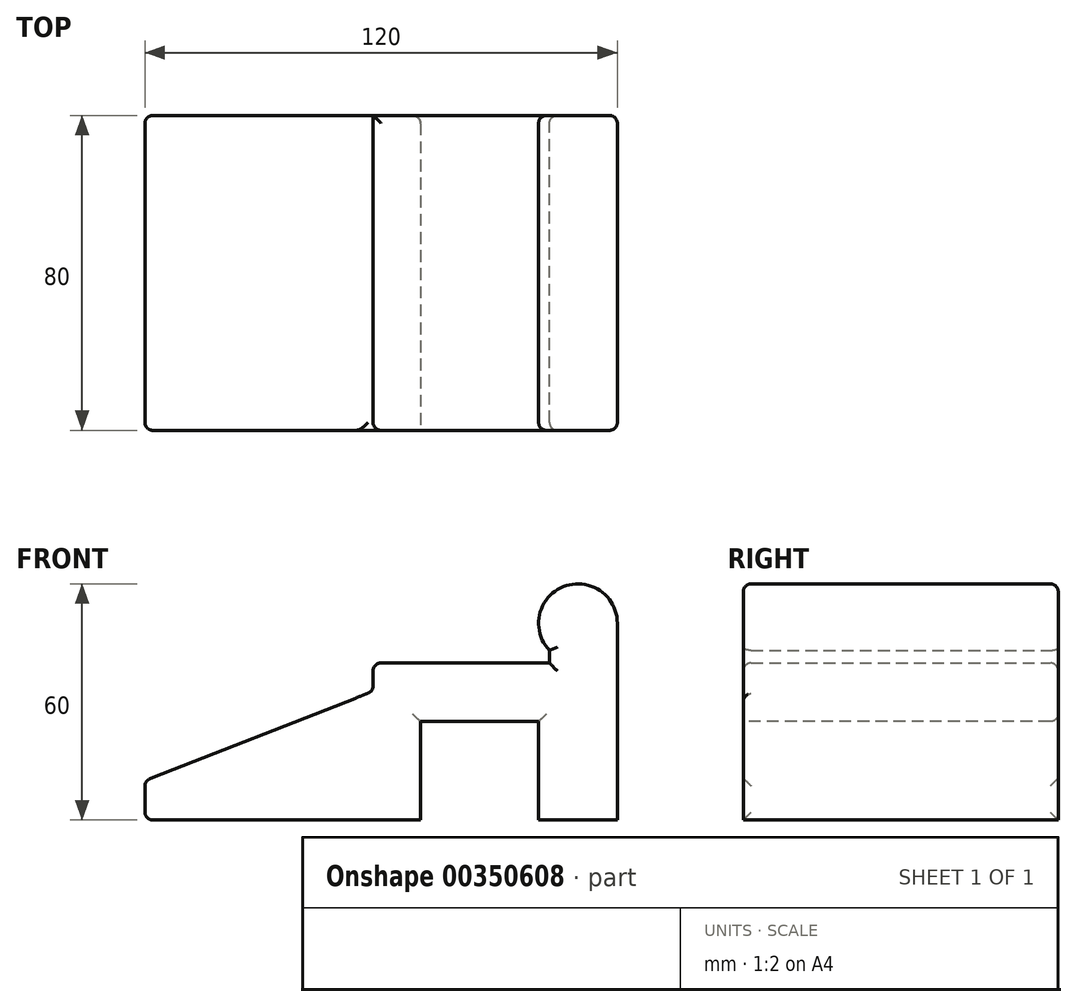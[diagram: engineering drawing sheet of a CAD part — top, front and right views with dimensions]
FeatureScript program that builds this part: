
annotation { "Feature Type Name" : "Feature", "Feature Type Description" : "" }
export const myFeature = defineFeature(function(context is Context, id is Id, definition is map)
    precondition{}
    {
        {
            var Q0;
            Q0=qCreatedBy(makeId("Front.planeOp"),FACE);
            var sketch = newSketch(context, id + "F0", { "sketchPlane" : qUnion([Q0])});
            skArc(sketch, "E0", {"start": v(112.98, 31.44) * mm, "mid": v(99.26, 40.72) * mm, "end": v(95.74, 24.54) * mm});
            skLineSegment(sketch, "E1", {"start": v(112.98, 31.44) * mm, "end": v(112.98, -18.56) * mm});
            skLineSegment(sketch, "E2", {"start": v(112.98, -18.56) * mm, "end": v(-7.02, -18.56) * mm});
            skLineSegment(sketch, "E3", {"start": v(-7.02, -8.56) * mm, "end": v(-7.02, -18.56) * mm});
            skLineSegment(sketch, "E4", {"start": v(95.74, 24.54) * mm, "end": v(95.74, 21.35) * mm});
            skLineSegment(sketch, "E5", {"start": v(50.93, 14.16) * mm, "end": v(50.93, 21.35) * mm});
            skLineSegment(sketch, "E6", {"start": v(50.93, 21.35) * mm, "end": v(95.74, 21.35) * mm});
            skLineSegment(sketch, "E7", {"start": v(-7.02, -8.56) * mm, "end": v(50.93, 14.16) * mm});
            skSolve(sketch);
        }
        {
            var Q0;
            Q0=makeQuery(id+"F0.imprint","IMPRINT",FACE,{"disambiguationData":[TD([[makeQuery(id+"F0.imprint","IMPRINT",EDGE,{"derivedFrom":sQuery(id+"F0.wireOp",EDGE,"E0")}),1.0]])]});
            extrude(context, id + "F1", {"entities" : qUnion([Q0]), "depth" : 80 * mm});
        }
        {
            var Q0;
            Q0=makeQuery(id+"F1.opExtrude","CAP_FACE",FACE,{"disambiguationData":[OSD([sQuery(id+"F0.wireOp",EDGE,"E0"),sQuery(id+"F0.wireOp",EDGE,"E1"),sQuery(id+"F0.wireOp",EDGE,"E2"),sQuery(id+"F0.wireOp",EDGE,"E3"),sQuery(id+"F0.wireOp",EDGE,"E4"),sQuery(id+"F0.wireOp",EDGE,"1WNvFodx-eBXk-6IQv-WaWy-YzUaJAq4HSbU"),sQuery(id+"F0.wireOp",EDGE,"E5"),sQuery(id+"F0.wireOp",EDGE,"E6")])],"isStart":false});
            var sketch = newSketch(context, id + "F2", { "sketchPlane" : qUnion([Q0])});
            skLineSegment(sketch, "E8.bottom", {"start": v(92.98, 6.44) * mm, "end": v(62.98, 6.44) * mm});
            skLineSegment(sketch, "E8.top", {"start": v(92.98, -18.56) * mm, "end": v(62.98, -18.56) * mm});
            skLineSegment(sketch, "E8.left", {"start": v(92.98, 6.44) * mm, "end": v(92.98, -18.56) * mm});
            skLineSegment(sketch, "E8.right", {"start": v(62.98, 6.44) * mm, "end": v(62.98, -18.56) * mm});
            skSolve(sketch);
        }
        {
            var Q0;
            Q0=makeQuery(id+"F2.imprint","IMPRINT",FACE,{"disambiguationData":[TD([[makeQuery(id+"F2.imprint","IMPRINT",EDGE,{"derivedFrom":sQuery(id+"F2.wireOp",EDGE,"E8.bottom")}),1.0]])]});
            extrude(context, id + "F3", {"entities" : qUnion([Q0]), "operationType" : NewBodyOperationType.REMOVE, "endBound" : BoundingType.THROUGH_ALL, "oppositeDirection" : true, "depth" : 25 * mm});
        }
        {
            var Q0;
            Q0=makeQuery(id+"F1.opExtrude","CAP_EDGE",EDGE,{"disambiguationData":[OSD([sQuery(id+"F0.wireOp",EDGE,"E6")])],"isStart":false});
            var Q1;
            Q1=makeQuery(id+"F1.opExtrude","CAP_EDGE",EDGE,{"disambiguationData":[OSD([sQuery(id+"F0.wireOp",EDGE,"E4")])],"isStart":false});
            var Q2;
            Q2=makeQuery(id+"F1.opExtrude","CAP_EDGE",EDGE,{"disambiguationData":[OSD([sQuery(id+"F0.wireOp",EDGE,"E0")])],"isStart":false});
            var Q3;
            Q3=makeQuery(id+"F3.boolean.opBoolean","COPY",EDGE,{"derivedFrom":makeQuery(id+"F3.opExtrude","CAP_EDGE",EDGE,{"disambiguationData":[OSD([sQuery(id+"F2.wireOp",EDGE,"E8.left")])],"isStart":true})});
            var Q4;
            Q4=makeQuery(id+"F3.boolean.opBoolean","COPY",EDGE,{"derivedFrom":makeQuery(id+"F3.opExtrude","CAP_EDGE",EDGE,{"disambiguationData":[OSD([sQuery(id+"F2.wireOp",EDGE,"E8.bottom")])],"isStart":true})});
            var Q5;
            Q5=makeQuery(id+"F3.boolean.opBoolean","COPY",EDGE,{"derivedFrom":makeQuery(id+"F3.opExtrude","CAP_EDGE",EDGE,{"disambiguationData":[OSD([sQuery(id+"F2.wireOp",EDGE,"E8.right")])],"isStart":true})});
            var Q6;
            Q6=makeQuery(id+"F1.opExtrude","CAP_EDGE",EDGE,{"disambiguationData":[OSD([sQuery(id+"F0.wireOp",EDGE,"1WNvFodx-eBXk-6IQv-WaWy-YzUaJAq4HSbU")])],"isStart":false});
            var Q7;
            Q7=makeQuery(id+"F1.opExtrude","CAP_EDGE",EDGE,{"disambiguationData":[OSD([sQuery(id+"F0.wireOp",EDGE,"E5")])],"isStart":false});
            var Q8;
            Q8=makeQuery(id+"F1.opExtrude","SWEPT_EDGE",EDGE,{"disambiguationData":[OSD([sQuery(id+"F0.wireOp",EDGE,"E3"),sQuery(id+"F0.wireOp",EDGE,"1WNvFodx-eBXk-6IQv-WaWy-YzUaJAq4HSbU")])]});
            var Q9;
            Q9=makeQuery(id+"F1.opExtrude","SWEPT_EDGE",EDGE,{"disambiguationData":[OSD([sQuery(id+"F0.wireOp",EDGE,"E5"),sQuery(id+"F0.wireOp",EDGE,"E6")])]});
            var Q10;
            Q10=makeQuery(id+"F1.opExtrude","SWEPT_EDGE",EDGE,{"disambiguationData":[OSD([sQuery(id+"F0.wireOp",EDGE,"1WNvFodx-eBXk-6IQv-WaWy-YzUaJAq4HSbU"),sQuery(id+"F0.wireOp",EDGE,"E5")])]});
            var Q11;
            Q11=makeQuery(id+"F1.opExtrude","CAP_EDGE",EDGE,{"disambiguationData":[OSD([sQuery(id+"F0.wireOp",EDGE,"1WNvFodx-eBXk-6IQv-WaWy-YzUaJAq4HSbU")])],"isStart":true});
            var Q12;
            Q12=makeQuery(id+"F1.opExtrude","CAP_EDGE",EDGE,{"disambiguationData":[OSD([sQuery(id+"F0.wireOp",EDGE,"E6")])],"isStart":true});
            var Q13;
            Q13=makeQuery(id+"F1.opExtrude","CAP_EDGE",EDGE,{"disambiguationData":[OSD([sQuery(id+"F0.wireOp",EDGE,"E3")])],"isStart":true});
            var Q14;
            Q14=makeQuery(id+"F3.boolean.opBoolean","INTERSECT",EDGE,{"derivedFrom":[makeQuery(id+"F1.opExtrude","CAP_FACE",FACE,{"disambiguationData":[OSD([sQuery(id+"F0.wireOp",EDGE,"E0"),sQuery(id+"F0.wireOp",EDGE,"E1"),sQuery(id+"F0.wireOp",EDGE,"E2"),sQuery(id+"F0.wireOp",EDGE,"E3"),sQuery(id+"F0.wireOp",EDGE,"E4"),sQuery(id+"F0.wireOp",EDGE,"1WNvFodx-eBXk-6IQv-WaWy-YzUaJAq4HSbU"),sQuery(id+"F0.wireOp",EDGE,"E5"),sQuery(id+"F0.wireOp",EDGE,"E6")])],"isStart":true}),makeQuery(id+"F3.opExtrude","SWEPT_FACE",FACE,{"disambiguationData":[OSD([sQuery(id+"F2.wireOp",EDGE,"E8.right")])]})]});
            var Q15;
            Q15=makeQuery(id+"F3.boolean.opBoolean","INTERSECT",EDGE,{"derivedFrom":[makeQuery(id+"F1.opExtrude","CAP_FACE",FACE,{"disambiguationData":[OSD([sQuery(id+"F0.wireOp",EDGE,"E0"),sQuery(id+"F0.wireOp",EDGE,"E1"),sQuery(id+"F0.wireOp",EDGE,"E2"),sQuery(id+"F0.wireOp",EDGE,"E3"),sQuery(id+"F0.wireOp",EDGE,"E4"),sQuery(id+"F0.wireOp",EDGE,"1WNvFodx-eBXk-6IQv-WaWy-YzUaJAq4HSbU"),sQuery(id+"F0.wireOp",EDGE,"E5"),sQuery(id+"F0.wireOp",EDGE,"E6")])],"isStart":true}),makeQuery(id+"F3.opExtrude","SWEPT_FACE",FACE,{"disambiguationData":[OSD([sQuery(id+"F2.wireOp",EDGE,"E8.bottom")])]})]});
            var Q16;
            Q16=makeQuery(id+"F3.boolean.opBoolean","INTERSECT",EDGE,{"derivedFrom":[makeQuery(id+"F1.opExtrude","CAP_FACE",FACE,{"disambiguationData":[OSD([sQuery(id+"F0.wireOp",EDGE,"E0"),sQuery(id+"F0.wireOp",EDGE,"E1"),sQuery(id+"F0.wireOp",EDGE,"E2"),sQuery(id+"F0.wireOp",EDGE,"E3"),sQuery(id+"F0.wireOp",EDGE,"E4"),sQuery(id+"F0.wireOp",EDGE,"1WNvFodx-eBXk-6IQv-WaWy-YzUaJAq4HSbU"),sQuery(id+"F0.wireOp",EDGE,"E5"),sQuery(id+"F0.wireOp",EDGE,"E6")])],"isStart":true}),makeQuery(id+"F3.opExtrude","SWEPT_FACE",FACE,{"disambiguationData":[OSD([sQuery(id+"F2.wireOp",EDGE,"E8.left")])]})]});
            var Q17;
            Q17=makeQuery(id+"F1.opExtrude","CAP_EDGE",EDGE,{"disambiguationData":[OSD([sQuery(id+"F0.wireOp",EDGE,"E4")])],"isStart":true});
            var Q18;
            Q18=makeQuery(id+"F1.opExtrude","CAP_EDGE",EDGE,{"disambiguationData":[OSD([sQuery(id+"F0.wireOp",EDGE,"E0")])],"isStart":true});
            var Q19;
            Q19=makeQuery(id+"F1.opExtrude","CAP_EDGE",EDGE,{"disambiguationData":[OSD([sQuery(id+"F0.wireOp",EDGE,"E3")])],"isStart":false});
            fillet(context, id + "F4", {"entities" : qUnion([Q0, Q1, Q2, Q3, Q4, Q5, Q6, Q7, Q8, Q9, Q10, Q11, Q12, Q13, Q14, Q15, Q16, Q17, Q18, Q19]), "radius" : 2 * mm, "tangentPropagation" : true, "allowEdgeOverflow" : false});
        }
    });
